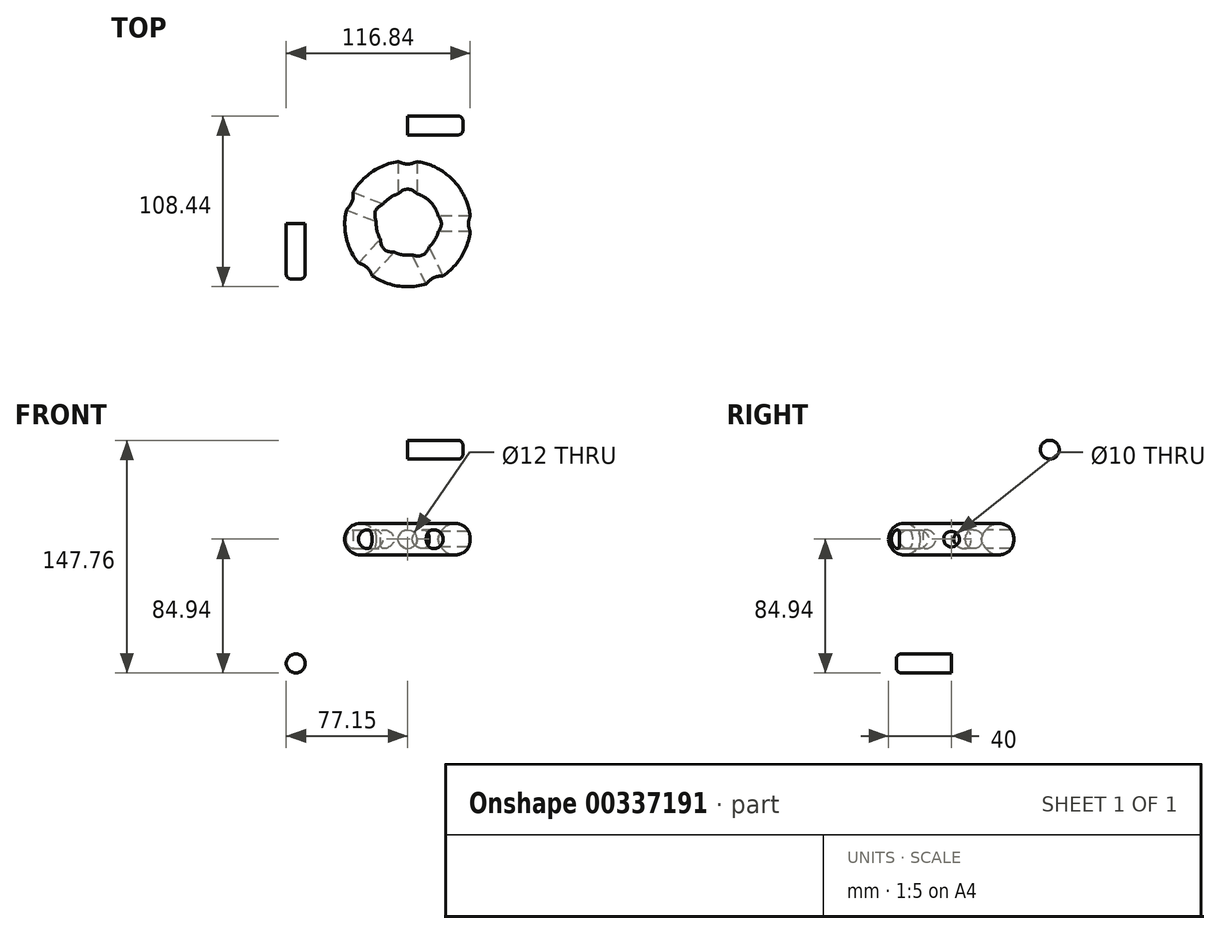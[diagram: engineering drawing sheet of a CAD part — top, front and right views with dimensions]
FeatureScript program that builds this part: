
annotation { "Feature Type Name" : "Feature", "Feature Type Description" : "" }
export const myFeature = defineFeature(function(context is Context, id is Id, definition is map)
    precondition{}
    {
        {
            var Q0;
            Q0=qCreatedBy(makeId("Top.planeOp"),FACE);
            var sketch = newSketch(context, id + "F0", { "sketchPlane" : qUnion([Q0])});
            skCircle(sketch, "E0", {"center": v(0, 0) * mm, "radius": 40 * mm});
            skCircle(sketch, "E1", {"center": v(0, 0) * mm, "radius": 20 * mm});
            skSolve(sketch);
        }
        {
            var Q0;
            Q0=makeQuery(id+"F0.imprint","IMPRINT",FACE,{"disambiguationData":[TD([[makeQuery(id+"F0.imprint","IMPRINT",EDGE,{"derivedFrom":sQuery(id+"F0.wireOp",EDGE,"E0")}),1.0]])]});
            extrude(context, id + "F1", {"entities" : qUnion([Q0]), "endBound" : BoundingType.SYMMETRIC, "depth" : 20 * mm});
        }
        {
            var Q0;
            Q0=makeQuery(id+"F1.opExtrude","CAP_EDGE",EDGE,{"disambiguationData":[OSD([sQuery(id+"F0.wireOp",EDGE,"E0")])],"isStart":true});
            var Q1;
            Q1=makeQuery(id+"F1.opExtrude","CAP_EDGE",EDGE,{"disambiguationData":[OSD([sQuery(id+"F0.wireOp",EDGE,"E1")])],"isStart":true});
            fillet(context, id + "F2", {"entities" : qUnion([Q0, Q1]), "radius" : 10 * mm, "tangentPropagation" : true, "allowEdgeOverflow" : false});
        }
        {
            var Q0;
            Q0=makeQuery(id+"F1.opExtrude","CAP_EDGE",EDGE,{"disambiguationData":[OSD([sQuery(id+"F0.wireOp",EDGE,"E0")])],"isStart":false});
            var Q1;
            Q1=makeQuery(id+"F1.opExtrude","CAP_EDGE",EDGE,{"disambiguationData":[OSD([sQuery(id+"F0.wireOp",EDGE,"E1")])],"isStart":false});
            fillet(context, id + "F3", {"entities" : qUnion([Q0, Q1]), "radius" : 10 * mm, "tangentPropagation" : true, "allowEdgeOverflow" : false});
        }
        {
            var Q0;
            Q0=qCreatedBy(makeId("Front.planeOp"),FACE);
            var sketch = newSketch(context, id + "F4", { "sketchPlane" : qUnion([Q0])});
            skCircle(sketch, "E2", {"center": v(0, 0) * mm, "radius": 6 * mm});
            skSolve(sketch);
        }
        {
            var Q0;
            Q0 = qSketchRegion(id + "F4", true);
            extrude(context, id + "F5", {"entities" : qUnion([Q0]), "oppositeDirection" : true, "depth" : 1000 * mm});
        }
        {
            var Q0;
            Q0=makeQuery(id+"F5.opExtrude","SWEPT_BODY",BODY,{"disambiguationData":[OSD([sQuery(id+"F4.wireOp",EDGE,"E2")])]});
            var Q1;
            Q1=makeQuery(id+"F2.opFillet","BLEND_FACE",FACE,{"disambiguationData":[OSD([sQuery(id+"F0.wireOp",EDGE,"E0")])]});
            circularPattern(context, id + "F6", {"operationType" : NewBodyOperationType.REMOVE, "entities" : qUnion([Q0]), "axis" : qUnion([Q1]), "angle" : 205.7 * degree, "instanceCount" : 4, "equalSpace" : true});
        }
        {
            var Q0;
            Q0=qCreatedBy(makeId("Front.planeOp"),FACE);
            var sketch = newSketch(context, id + "F7", { "sketchPlane" : qUnion([Q0])});
            skCircle(sketch, "E3", {"center": v(-71.15, -78.94) * mm, "radius": 6 * mm});
            skPoint(sketch, "E3.first.point", {"position": v(-72.25, -73.04) * mm});
            skPoint(sketch, "E3.second.point", {"position": v(-74.28, -73.82) * mm});
            skPoint(sketch, "E3.third.point", {"position": v(-76.47, -76.16) * mm});
            skSolve(sketch);
        }
        {
            var Q0;
            Q0=makeQuery(id+"F7.imprint","IMPRINT",FACE,{"disambiguationData":[TD([[makeQuery(id+"F7.imprint","IMPRINT",EDGE,{"derivedFrom":sQuery(id+"F7.wireOp",EDGE,"E3")}),1.0]])]});
            extrude(context, id + "F8", {"entities" : qUnion([Q0]), "depth" : 35 * mm});
        }
        {
            var Q0;
            Q0=makeQuery(id+"F8.opExtrude","CAP_EDGE",EDGE,{"disambiguationData":[OSD([sQuery(id+"F7.wireOp",EDGE,"E3")])],"isStart":false});
            fillet(context, id + "F9", {"entities" : qUnion([Q0]), "radius" : 3 * mm, "tangentPropagation" : true, "allowEdgeOverflow" : false});
        }
        {
            var Q0;
            Q0=qCreatedBy(makeId("Right.planeOp"),FACE);
            var sketch = newSketch(context, id + "F10", { "sketchPlane" : qUnion([Q0])});
            skCircle(sketch, "E4", {"center": v(62.44, 56.82) * mm, "radius": 6 * mm});
            skPoint(sketch, "E4.first.point", {"position": v(56.73, 55) * mm});
            skPoint(sketch, "E4.second.point", {"position": v(60.62, 51.1) * mm});
            skPoint(sketch, "E4.third.point", {"position": v(67.55, 59.98) * mm});
            skSolve(sketch);
        }
        {
            var Q0;
            Q0=makeQuery(id+"F10.imprint","IMPRINT",FACE,{"disambiguationData":[TD([[makeQuery(id+"F10.imprint","IMPRINT",EDGE,{"derivedFrom":sQuery(id+"F10.wireOp",EDGE,"E4")}),1.0]])]});
            extrude(context, id + "F11", {"entities" : qUnion([Q0]), "depth" : 35 * mm});
        }
        {
            var Q0;
            Q0=makeQuery(id+"F11.opExtrude","CAP_EDGE",EDGE,{"disambiguationData":[OSD([sQuery(id+"F10.wireOp",EDGE,"E4")])],"isStart":false});
            fillet(context, id + "F12", {"entities" : qUnion([Q0]), "radius" : 3 * mm, "tangentPropagation" : true, "allowEdgeOverflow" : false});
        }
        {
            var Q0;
            Q0=qCreatedBy(makeId("Right.planeOp"),FACE);
            var sketch = newSketch(context, id + "F13", { "sketchPlane" : qUnion([Q0])});
            skCircle(sketch, "E5", {"center": v(0, 0) * mm, "radius": 5 * mm});
            skSolve(sketch);
        }
        {
            var Q0;
            Q0 = qSketchRegion(id + "F13", true);
            extrude(context, id + "F14", {"entities" : qUnion([Q0]), "operationType" : NewBodyOperationType.REMOVE, "oppositeDirection" : true, "depth" : -100 * mm});
        }
    });
